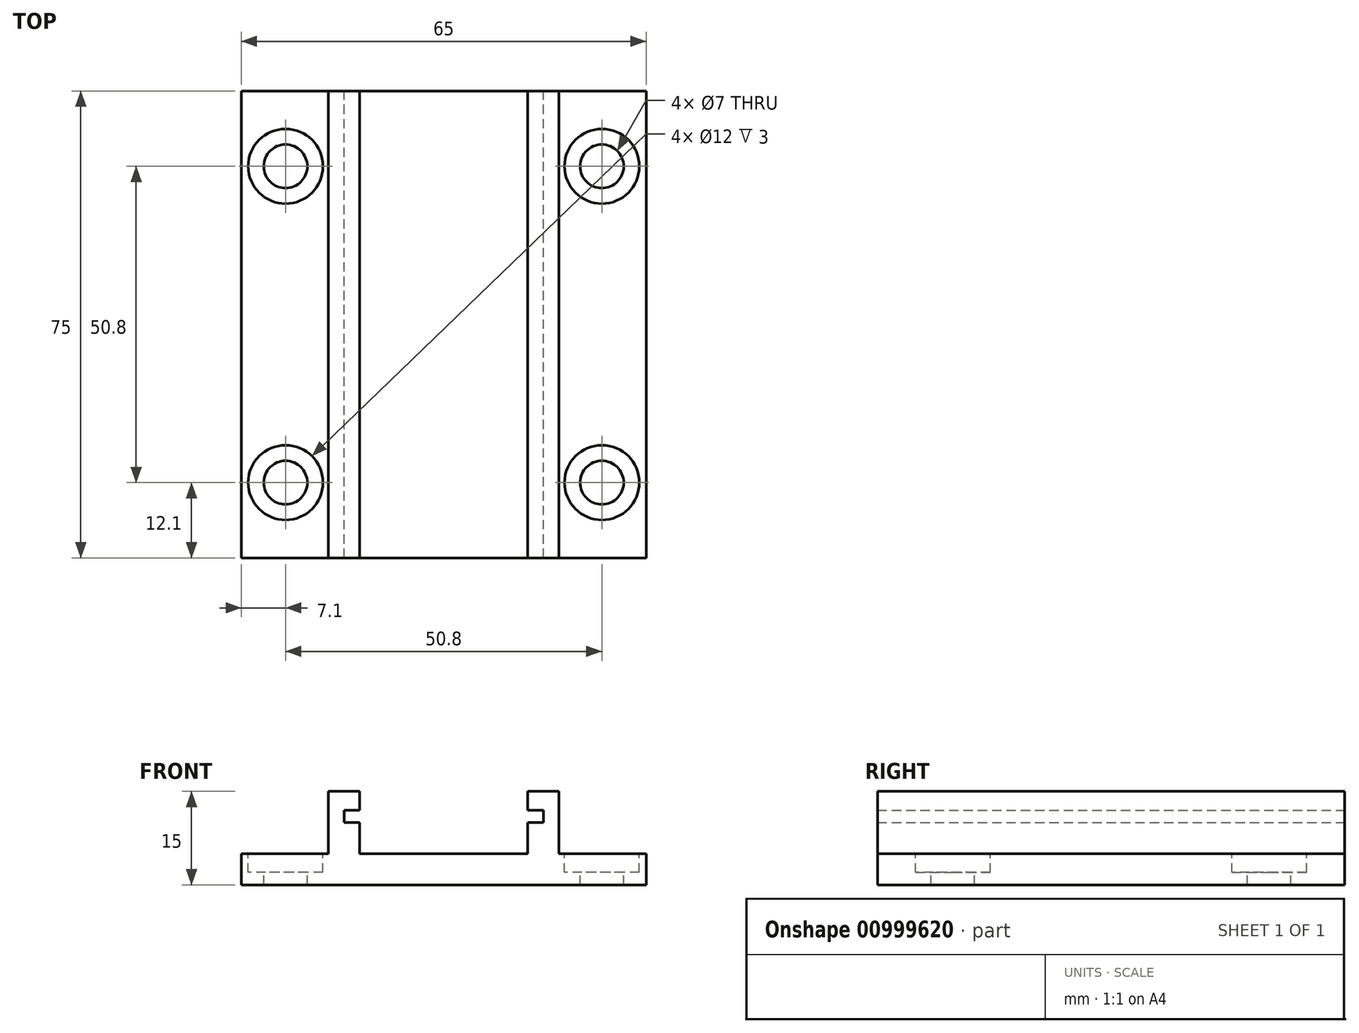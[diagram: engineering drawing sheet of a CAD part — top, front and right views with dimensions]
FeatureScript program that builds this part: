
annotation { "Feature Type Name" : "Feature", "Feature Type Description" : "" }
export const myFeature = defineFeature(function(context is Context, id is Id, definition is map)
    precondition{}
    {
        {
            var Q0;
            Q0=qCreatedBy(makeId("Front.planeOp"),FACE);
            var sketch = newSketch(context, id + "F0", { "sketchPlane" : qUnion([Q0])});
            skLineSegment(sketch, "E0", {"start": v(0, 25.1) * mm, "end": v(0, -21.2) * mm, "construction": true});
            skLineSegment(sketch, "E1", {"start": v(-22.5, 0) * mm, "end": v(23.02, 0) * mm, "construction": true});
            skLineSegment(sketch, "E2", {"start": v(0, 0) * mm, "end": v(-32.5, 0) * mm});
            skLineSegment(sketch, "E3", {"start": v(-32.5, 0) * mm, "end": v(-32.5, 5) * mm});
            skLineSegment(sketch, "E4", {"start": v(-32.5, 5) * mm, "end": v(-18.5, 5) * mm});
            skLineSegment(sketch, "E5", {"start": v(-18.5, 5) * mm, "end": v(-18.5, 15) * mm});
            skLineSegment(sketch, "E6", {"start": v(-18.5, 15) * mm, "end": v(-13.5, 15) * mm});
            skLineSegment(sketch, "E7", {"start": v(-13.5, 15) * mm, "end": v(-13.5, 12) * mm});
            skLineSegment(sketch, "E8", {"start": v(-13.5, 12) * mm, "end": v(-16, 12) * mm});
            skLineSegment(sketch, "E9", {"start": v(-16, 12) * mm, "end": v(-16, 10) * mm});
            skLineSegment(sketch, "E10", {"start": v(-16, 10) * mm, "end": v(-13.5, 10) * mm});
            skLineSegment(sketch, "E11", {"start": v(-13.5, 10) * mm, "end": v(-13.5, 5) * mm});
            skLineSegment(sketch, "E12", {"start": v(-13.5, 5) * mm, "end": v(0, 5) * mm});
            skLineSegment(sketch, "E13.MirrorCS", {"start": v(13.5, 5) * mm, "end": v(0, 5) * mm});
            skLineSegment(sketch, "E14.MirrorCS", {"start": v(18.5, 15) * mm, "end": v(13.5, 15) * mm});
            skLineSegment(sketch, "E15.MirrorCS", {"start": v(0, 0) * mm, "end": v(32.5, 0) * mm});
            skLineSegment(sketch, "E16.MirrorCS", {"start": v(18.5, 5) * mm, "end": v(18.5, 15) * mm});
            skLineSegment(sketch, "E17.MirrorCS", {"start": v(13.5, 15) * mm, "end": v(13.5, 12) * mm});
            skLineSegment(sketch, "E18.MirrorCS", {"start": v(13.5, 12) * mm, "end": v(16, 12) * mm});
            skLineSegment(sketch, "E19.MirrorCS", {"start": v(13.5, 10) * mm, "end": v(13.5, 5) * mm});
            skLineSegment(sketch, "E20.MirrorCS", {"start": v(16, 10) * mm, "end": v(13.5, 10) * mm});
            skLineSegment(sketch, "E21.MirrorCS", {"start": v(32.5, 5) * mm, "end": v(18.5, 5) * mm});
            skLineSegment(sketch, "E22.MirrorCS", {"start": v(32.5, 0) * mm, "end": v(32.5, 5) * mm});
            skLineSegment(sketch, "E23.MirrorCS", {"start": v(16, 12) * mm, "end": v(16, 10) * mm});
            skSolve(sketch);
        }
        {
            var Q0;
            Q0=makeQuery(id+"F0.imprint","IMPRINT",FACE,{"disambiguationData":[TD([[makeQuery(id+"F0.imprint","IMPRINT",EDGE,{"derivedFrom":sQuery(id+"F0.wireOp",EDGE,"E2")}),-1.0]])]});
            extrude(context, id + "F1", {"entities" : qUnion([Q0]), "depth" : 75 * mm, "offsetDistance" : 25 * mm});
        }
        {
            var Q0;
            Q0=makeQuery(id+"F1.opExtrude","SWEPT_FACE",FACE,{"disambiguationData":[OSD([sQuery(id+"F0.wireOp",EDGE,"E4")])]});
            var sketch = newSketch(context, id + "F2", { "sketchPlane" : qUnion([Q0])});
            skLineSegment(sketch, "E24", {"start": v(0, 0) * mm, "end": v(0, -88.94) * mm, "construction": true});
            skLineSegment(sketch, "E25", {"start": v(-32.5, -37.5) * mm, "end": v(34.35, -37.5) * mm, "construction": true});
            skPoint(sketch, "E26", {"position": v(-25.4, -62.9) * mm});
            skPoint(sketch, "E27", {"position": v(-25.4, -12.1) * mm});
            skPoint(sketch, "E28", {"position": v(25.4, -12.1) * mm});
            skPoint(sketch, "E29", {"position": v(25.4, -62.9) * mm});
            skSolve(sketch);
        }
        {
            var Q0;
            Q0=sQuery(id+"F2.wireOp",VERTEX,"E27");
            var Q1;
            Q1=sQuery(id+"F2.wireOp",VERTEX,"E26");
            var Q2;
            Q2=sQuery(id+"F2.wireOp",VERTEX,"E29");
            var Q3;
            Q3=sQuery(id+"F2.wireOp",VERTEX,"E28");
            var Q4;
            Q4=makeQuery(id+"F1.opExtrude","SWEPT_BODY",BODY,{"disambiguationData":[OSD([sQuery(id+"F0.wireOp",EDGE,"E2"),sQuery(id+"F0.wireOp",EDGE,"E3"),sQuery(id+"F0.wireOp",EDGE,"E4"),sQuery(id+"F0.wireOp",EDGE,"E5"),sQuery(id+"F0.wireOp",EDGE,"E6"),sQuery(id+"F0.wireOp",EDGE,"E7"),sQuery(id+"F0.wireOp",EDGE,"E8"),sQuery(id+"F0.wireOp",EDGE,"E9"),sQuery(id+"F0.wireOp",EDGE,"E10"),sQuery(id+"F0.wireOp",EDGE,"E11"),sQuery(id+"F0.wireOp",EDGE,"E12"),sQuery(id+"F0.wireOp",EDGE,"E13.MirrorCS"),sQuery(id+"F0.wireOp",EDGE,"E14.MirrorCS"),sQuery(id+"F0.wireOp",EDGE,"E15.MirrorCS"),sQuery(id+"F0.wireOp",EDGE,"E16.MirrorCS"),sQuery(id+"F0.wireOp",EDGE,"E17.MirrorCS"),sQuery(id+"F0.wireOp",EDGE,"E18.MirrorCS"),sQuery(id+"F0.wireOp",EDGE,"E19.MirrorCS"),sQuery(id+"F0.wireOp",EDGE,"E20.MirrorCS"),sQuery(id+"F0.wireOp",EDGE,"E21.MirrorCS"),sQuery(id+"F0.wireOp",EDGE,"E22.MirrorCS"),sQuery(id+"F0.wireOp",EDGE,"E23.MirrorCS")])]});
            hole(context, id + "F3", {"style" : HoleStyle.C_BORE, "endStyle" : HoleEndStyle.THROUGH, "holeDiameter" : 7 * mm, "cBoreDiameter" : 12 * mm, "cBoreDepth" : 3 * mm, "majorDiameter" : 5 * mm, "isTappedThrough" : true, "tappedDepth" : 12 * mm, "tapClearance" : 3, "startFromSketch" : true, "locations" : qUnion([Q0, Q1, Q2, Q3]), "scope" : qUnion([Q4])});
        }
    });
